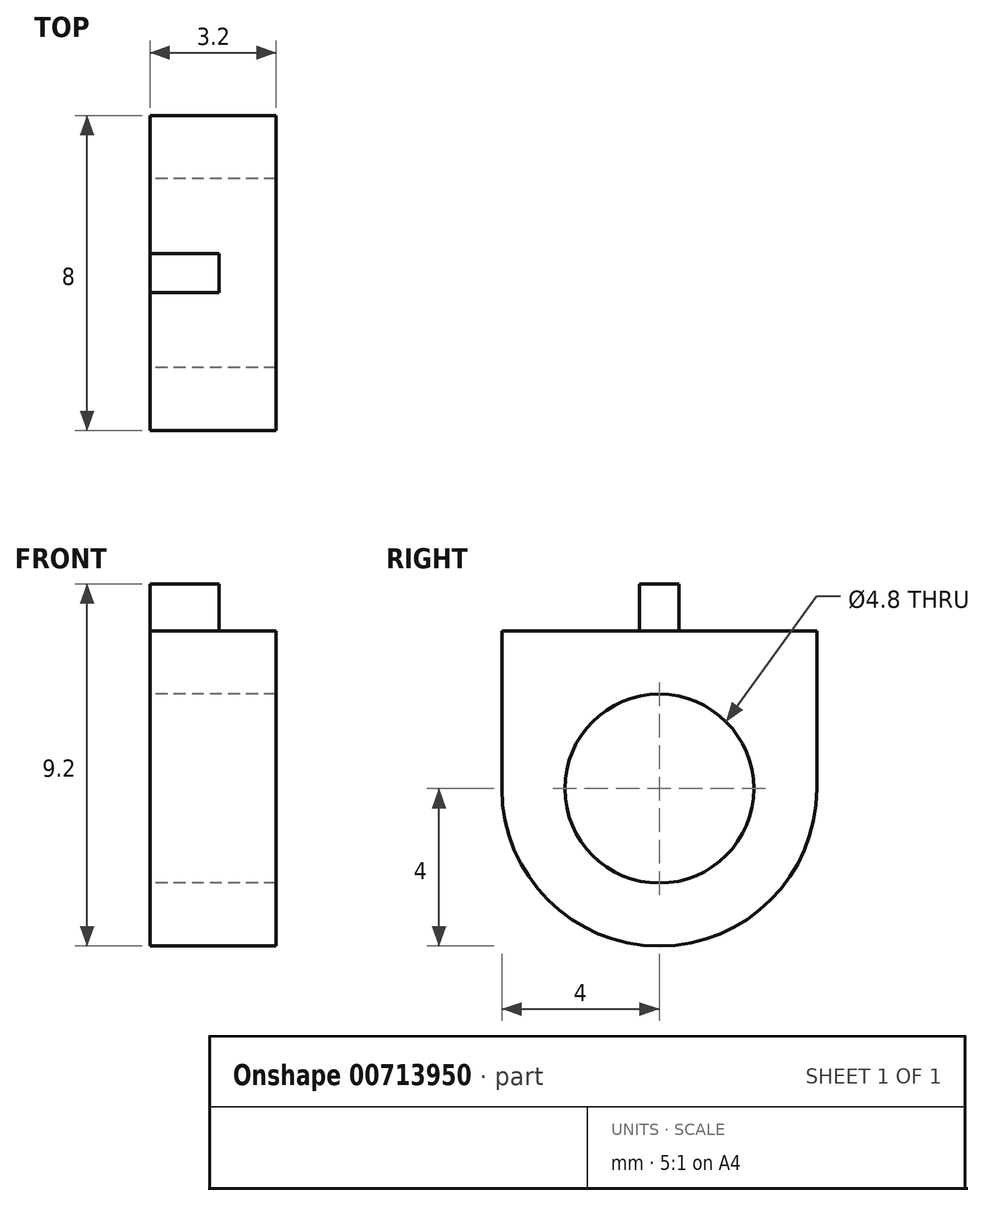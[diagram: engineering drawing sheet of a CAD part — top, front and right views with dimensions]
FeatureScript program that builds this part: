
annotation { "Feature Type Name" : "Feature", "Feature Type Description" : "" }
export const myFeature = defineFeature(function(context is Context, id is Id, definition is map)
    precondition{}
    {
        {
            var Q0;
            Q0=qCreatedBy(makeId("Right.planeOp"),FACE);
            var sketch = newSketch(context, id + "F0", { "sketchPlane" : qUnion([Q0]), "disableImprinting" : false});
            skLineSegment(sketch, "E0.bottom", {"start": v(4, -4) * mm, "end": v(-4, -4) * mm});
            skLineSegment(sketch, "E0.top", {"start": v(4, 4) * mm, "end": v(-4, 4) * mm});
            skLineSegment(sketch, "E0.left", {"start": v(4, -4) * mm, "end": v(4, 4) * mm});
            skLineSegment(sketch, "E0.right", {"start": v(-4, -4) * mm, "end": v(-4, 4) * mm});
            skPoint(sketch, "E0.middle", {"position": v(0, 0) * mm});
            skCircle(sketch, "E1", {"center": v(0, 0) * mm, "radius": 2.4 * mm});
            skSolve(sketch);
        }
        {
            var Q0;
            Q0=makeQuery(id+"F0.imprint","IMPRINT",FACE,{"disambiguationData":[TD([[makeQuery(id+"F0.imprint","IMPRINT",EDGE,{"derivedFrom":sQuery(id+"F0.wireOp",EDGE,"E0.bottom")}),-1.0]])]});
            extrude(context, id + "F1", {"entities" : qUnion([Q0]), "depth" : 3.2 * mm, "offsetDistance" : 25 * mm});
        }
        {
            var Q0;
            Q0=makeQuery(id+"F1.opExtrude","SWEPT_FACE",FACE,{"disambiguationData":[OSD([sQuery(id+"F0.wireOp",EDGE,"E0.top")])]});
            var sketch = newSketch(context, id + "F2", { "sketchPlane" : qUnion([Q0])});
            skLineSegment(sketch, "E2.bottom", {"start": v(1.75, 0.5) * mm, "end": v(-1.75, 0.5) * mm});
            skLineSegment(sketch, "E2.top", {"start": v(1.75, -0.5) * mm, "end": v(-1.75, -0.5) * mm});
            skLineSegment(sketch, "E2.left", {"start": v(1.75, 0.5) * mm, "end": v(1.75, -0.5) * mm});
            skLineSegment(sketch, "E2.right", {"start": v(-1.75, 0.5) * mm, "end": v(-1.75, -0.5) * mm});
            skPoint(sketch, "E2.middle", {"position": v(0, 0) * mm});
            skSolve(sketch);
        }
        {
            var Q0;
            {var subQ0=sQuery(id+"F2.wireOp",EDGE,"E2.left");Q0=makeQuery(id+"F2.imprint","IMPRINT",FACE,{"disambiguationData":[TD([[makeQuery(id+"F2.imprint","IMPRINT",EDGE,{"derivedFrom":subQ0}),-1.0]])]});}
            extrude(context, id + "F3", {"entities" : qUnion([Q0]), "operationType" : NewBodyOperationType.ADD, "depth" : 1.2 * mm, "offsetDistance" : 25 * mm});
        }
        {
            var Q0;
            Q0=makeQuery(id+"F1.opExtrude","SWEPT_EDGE",EDGE,{"disambiguationData":[OSD([sQuery(id+"F0.wireOp",EDGE,"E0.bottom"),sQuery(id+"F0.wireOp",EDGE,"E0.right")])]});
            var Q1;
            Q1=makeQuery(id+"F1.opExtrude","SWEPT_EDGE",EDGE,{"disambiguationData":[OSD([sQuery(id+"F0.wireOp",EDGE,"E0.bottom"),sQuery(id+"F0.wireOp",EDGE,"E0.left")])]});
            fillet(context, id + "F4", {"entities" : qUnion([Q0, Q1]), "radius" : 4 * mm, "tangentPropagation" : true, "allowEdgeOverflow" : false});
        }
    });
